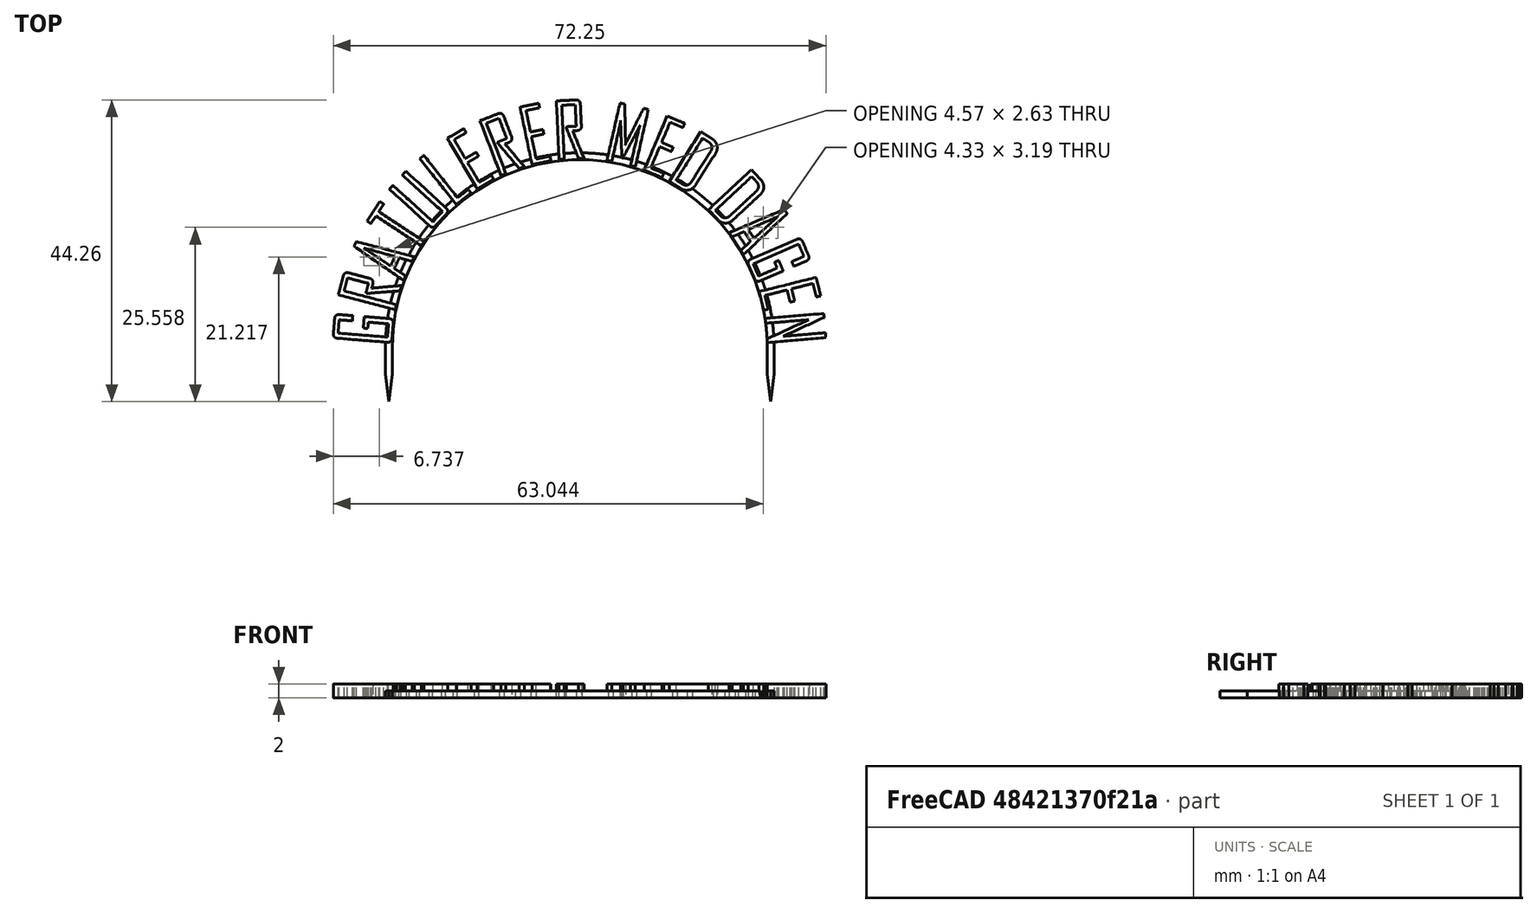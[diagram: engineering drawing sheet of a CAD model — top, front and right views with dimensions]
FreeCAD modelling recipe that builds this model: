
FCSTD DOCUMENT  (FreeCAD 0.20R29177 (Git))
Label: cake-topper-buon-compleanno
License: All rights reserved
LicenseURL: http://en.wikipedia.org/wiki/All_rights_reserved
objects: Part::Feature×22, Sketcher::SketchObject×4, PartDesign::Pad×4, App::DocumentObjectGroup×3, App::TextDocument×1, Spreadsheet::Sheet×1, PartDesign::Plane×1, PartDesign::Body×1, Mesh::Feature×1
note: 36 computed .brp shape members not serialized (recipe doc carries the construction recipe); baked Part::Feature solids carry a one-line shape summary decoded from their .brp

FEATURE [App::TextDocument] Text_document  label="Text document"
FEATURE [Spreadsheet::Sheet] Spreadsheet
  cells = A1=Text height; B1=text_h; C1(dim_text_h)==2mm; A2=Text offset x; B2=text_x; C2(dim_text_x)==-105.3mm; A3=Text offset y; B3=text_y; C3(dim_text_y)==177.4mm; A4=Scaffold height; B4=scaffold_h; C4(dim_scaffold_h)==1mm; A5=Scaffold width; B5=scaffold_w; C5(dim_scaffold_w)==1mm; A6=Scaffold inner radius; B6=scaffold_ir; C6(dim_scaffold_ir)==27.5mm; A7=Scaffold outer radius; B7=scaffold_or; C7(dim_scaffold_or)==dim_scaffold_ir + dim_scaffold_w; A8=Tines length; B8=tine_l; C8(dim_tine_l)==4mm; A9=Tines shaft length; B9=tine_shaft_l; C9(dim_tine_shaft_l)==4mm
FEATURE [PartDesign::Plane] DatumPlane  label="BaseXYDatumPlane"
  Length = 85.5553
  MapMode = 5
  ResizeMode = 0
  Support = -> [XY_Plane]
  Width = 74.5697
FEATURE [Sketcher::SketchObject] Sketch001  label="ArcSketch"
  FullyConstrained = true
  MapMode = 5
  Support = -> [DatumPlane]
  expr: Constraints[15] = Spreadsheet.dim_scaffold_or
  expr: Constraints[38] = Spreadsheet.dim_tine_shaft_l
  expr: Constraints[39] = Spreadsheet.dim_tine_l
  expr: Constraints[65] = Spreadsheet.dim_scaffold_or
  expr: Constraints[6] = Spreadsheet.dim_scaffold_ir
  sketch-geometry (26):
    g0: ArcOfCircle CenterX=0 CenterY=0 CenterZ=0 NormalX=0 NormalY=0 NormalZ=1 AngleXU=0 Radius=27.5 StartAngle=0 EndAngle=3.14159
    g1: LineSegment StartX=-28.5 StartY=3.5e-15 StartZ=0 EndX=-27.5 EndY=3.4e-15 EndZ=0
    g2: LineSegment StartX=27.5 StartY=0 StartZ=0 EndX=28.5 EndY=0 EndZ=0
    g3: ArcOfCircle CenterX=0 CenterY=0 CenterZ=0 NormalX=0 NormalY=0 NormalZ=1 AngleXU=0 Radius=28.5 StartAngle=1.44096 EndAngle=3.14159
    g4: ArcOfCircle CenterX=0 CenterY=0 CenterZ=0 NormalX=0 NormalY=0 NormalZ=1 AngleXU=0 Radius=28.5 StartAngle=0 EndAngle=1.40587
    g5: ArcOfCircle CenterX=0 CenterY=0 CenterZ=0 NormalX=0 NormalY=0 NormalZ=1 AngleXU=0 Radius=28.5 StartAngle=1.40587 EndAngle=1.44096
    g6: LineSegment StartX=3.69 StartY=28.2601 StartZ=0 EndX=5.12878 EndY=38.3822 EndZ=0
    g7: LineSegment StartX=4.67918 StartY=28.1133 StartZ=0 EndX=6.11883 EndY=38.2415 EndZ=0
    g8: LineSegment StartX=5.12878 StartY=38.3822 StartZ=0 EndX=6.11883 EndY=38.2415 EndZ=0
    g9: LineSegment StartX=-28.5 StartY=3.5e-15 StartZ=0 EndX=-28.5 EndY=-4 EndZ=0
    g10: LineSegment StartX=-27.5 StartY=3.4e-15 StartZ=0 EndX=-27.5 EndY=-4 EndZ=0
    g11: LineSegment StartX=-28.5 StartY=-4 StartZ=0 EndX=-28 EndY=-8 EndZ=0
    g12: LineSegment StartX=-27.5 StartY=-4 StartZ=0 EndX=-28 EndY=-8 EndZ=0
    g13: LineSegment StartX=-28.5 StartY=-4 StartZ=0 EndX=-28 EndY=-4 EndZ=0
    g14: LineSegment StartX=-28 StartY=-4 StartZ=0 EndX=-27.5 EndY=-4 EndZ=0
    g15: LineSegment StartX=-28 StartY=-4 StartZ=0 EndX=-28 EndY=-8 EndZ=0
    g16: LineSegment StartX=27.5 StartY=-4 StartZ=0 EndX=28 EndY=-4 EndZ=0
    g17: LineSegment StartX=28 StartY=-4 StartZ=0 EndX=28.5 EndY=-4 EndZ=0
    g18: LineSegment StartX=28 StartY=-4 StartZ=0 EndX=28 EndY=-8 EndZ=0
    g19: LineSegment StartX=27.5 StartY=0 StartZ=0 EndX=27.5 EndY=-4 EndZ=0
    g20: LineSegment StartX=28.5 StartY=0 StartZ=0 EndX=28.5 EndY=-4 EndZ=0
    g21: LineSegment StartX=27.5 StartY=-4 StartZ=0 EndX=28 EndY=-8 EndZ=0
    g22: LineSegment StartX=28.5 StartY=-4 StartZ=0 EndX=28 EndY=-8 EndZ=0
    g23: LineSegment StartX=3.69 StartY=28.2601 StartZ=0 EndX=0 EndY=28.2601 EndZ=0
    g24: LineSegment StartX=28.5 StartY=0 StartZ=0 EndX=28.5 EndY=28.5 EndZ=0
    g25: LineSegment StartX=28.5 StartY=28.5 StartZ=0 EndX=4.73415 EndY=28.5 EndZ=0
  constraints (71):
    c: Coincident(g0,g-1)
    c: PointOnObject(g0,g-1)
    c: PointOnObject(g0,g-1)
    c: Coincident(g4,g0)
    c: PointOnObject(g3,g-1)
    c: PointOnObject(g4,g-1)
    c: Radius(g0) = 27.5
    c: Coincident(g1,g3)
    c: Coincident(g1,g0)
    c: Coincident(g2,g0)
    c: Coincident(g2,g4)
    c: Coincident(g5,g3)
    c: Coincident(g4,g3)
    c: Coincident(g4,g5)
    c: Coincident(g4,g5)
    c: Radius(g4) = 28.5
    c: Coincident(g6,g3)
    c: Coincident(g7,g4)
    c: Coincident(g8,g6)
    c: Coincident(g8,g7)
    c: Parallel(g6,g7)
    c: Perpendicular(g8,g6)
    c: Coincident(g9,g3)
    c: Vertical(g9)
    c: Coincident(g10,g0)
    c: Vertical(g10)
    c: Coincident(g11,g9)
    c: Coincident(g12,g10)
    c: Coincident(g12,g11)
    c: Coincident(g13,g9)
    c: Horizontal(g13)
    c: Coincident(g14,g13)
    c: Coincident(g14,g10)
    c: Horizontal(g14)
    c: Coincident(g15,g13)
    c: Coincident(g15,g11)
    c: Equal(g14,g13)
    c: Vertical(g15)
    c: DistanceY(g10,g10) = 4
    c: DistanceY(g11,g10) = 4
    c: Horizontal(g16)
    c: Coincident(g17,g16)
    c: Horizontal(g17)
    c: Coincident(g18,g16)
    c: Vertical(g18)
    c: Coincident(g19,g0)
    c: Coincident(g19,g16)
    c: Vertical(g19)
    c: Coincident(g20,g4)
    c: Coincident(g20,g17)
    c: Vertical(g20)
    c: Coincident(g21,g19)
    c: Coincident(g21,g18)
    c: Coincident(g22,g20)
    c: Coincident(g22,g21)
    c: Equal(g19,g10)
    c: Equal(g18,g15)
    c: Equal(g17,g16)
    c: Distance(g8) = 1
    c: Coincident(g23,g3)
    c: PointOnObject(g23,g-2)
    c: Horizontal(g23)
    c: DistanceX(g23,g23) = 3.69
    c: Coincident(g24,g4)
    c: Vertical(g24)
    c: DistanceY(g24,g24) = 28.5
    c: Coincident(g25,g24)
    c: PointOnObject(g25,g7)
    c: Horizontal(g25)
    c: Angle(g25,g7) = 1.4296
    c: Distance(g7) = 10.23
FEATURE [PartDesign::Pad] Pad  label="ArcPad"
  Direction = (0,0,1)
  Length = 1
  Length2 = 10
  Profile = -> Sketch001
  ReferenceAxis = -> Sketch001 [N_Axis]
  Type = 0
  expr: Length = Spreadsheet.dim_scaffold_h
FEATURE [Part::Feature] path26706
  shape: bbox 8.818 x 4.113 x 2e-07 mm, 0 faces, 0 solids (baked)
FEATURE [Part::Feature] path26708
  shape: bbox 9.277 x 5.465 x 2e-07 mm, 0 faces, 0 solids (baked)
FEATURE [Part::Feature] path26710
  shape: bbox 8.816 x 5.676 x 2e-07 mm, 0 faces, 0 solids (baked)
FEATURE [Part::Feature] path26710001
  shape: bbox 4.566 x 2.632 x 2e-07 mm, 0 faces, 0 solids (baked)
FEATURE [Part::Feature] path26712
  shape: bbox 8.371 x 6.488 x 2e-07 mm, 0 faces, 0 solids (baked)
FEATURE [Part::Feature] path26714
  shape: bbox 8.547 x 8.23 x 2e-07 mm, 0 faces, 0 solids (baked)
FEATURE [Part::Feature] path26716
  shape: bbox 7.527 x 7.228 x 2e-07 mm, 0 faces, 0 solids (baked)
FEATURE [Part::Feature] path26718
  shape: bbox 6.804 x 8.859 x 2e-07 mm, 0 faces, 0 solids (baked)
FEATURE [Part::Feature] path26720
  shape: bbox 6.53 x 9.155 x 2e-07 mm, 0 faces, 0 solids (baked)
FEATURE [Part::Feature] path26722
  shape: bbox 4.54 x 9.017 x 2e-07 mm, 0 faces, 0 solids (baked)
FEATURE [Part::Feature] path26724
  shape: bbox 4.063 x 8.762 x 2e-07 mm, 0 faces, 0 solids (baked)
FEATURE [App::DocumentObjectGroup] Group  label="GratulererGroup"
  Group = -> [path26706,path26708,path26710,path26710001,path26712,path26714,path26716,path26718,path26720,path26722,path26724]
FEATURE [Part::Feature] path26726
  shape: bbox 6.071 x 9.357 x 2e-07 mm, 0 faces, 0 solids (baked)
FEATURE [Part::Feature] path26728
  shape: bbox 5.942 x 9.049 x 2e-07 mm, 0 faces, 0 solids (baked)
FEATURE [Part::Feature] path26730
  shape: bbox 7.088 x 8.663 x 2e-07 mm, 0 faces, 0 solids (baked)
FEATURE [Part::Feature] path26730001
  shape: bbox 5.278 x 6.906 x 2e-07 mm, 0 faces, 0 solids (baked)
FEATURE [App::DocumentObjectGroup] Group001  label="medGroup"
  Group = -> [path26726,path26728,path26730,path26730001]
FEATURE [Part::Feature] path26732
  shape: bbox 8.126 x 7.885 x 2e-07 mm, 0 faces, 0 solids (baked)
FEATURE [Part::Feature] path26732001
  shape: bbox 6.334 x 6.087 x 2e-07 mm, 0 faces, 0 solids (baked)
FEATURE [Part::Feature] path26734
  shape: bbox 8.492 x 6.647 x 2e-07 mm, 0 faces, 0 solids (baked)
FEATURE [Part::Feature] path26734001
  shape: bbox 4.328 x 3.192 x 2e-07 mm, 0 faces, 0 solids (baked)
FEATURE [Part::Feature] path26736
  shape: bbox 8.97 x 6.298 x 2e-07 mm, 0 faces, 0 solids (baked)
FEATURE [Part::Feature] path26738
  shape: bbox 9.049 x 4.849 x 2e-07 mm, 0 faces, 0 solids (baked)
FEATURE [Part::Feature] path26740
  shape: bbox 8.892 x 4.259 x 2e-07 mm, 0 faces, 0 solids (baked)
FEATURE [App::DocumentObjectGroup] Group002  label="dagenGroup"
  Group = -> [path26732,path26732001,path26734,path26734001,path26736,path26738,path26740]
FEATURE [Sketcher::SketchObject] Sketch  label="GratulererSketch"
  FullyConstrained = false
  Placement = pos=(-105.3,177.4,0) rot=(0,0,1;0rad)
  expr: .Placement.Base.x = Spreadsheet.dim_text_x
  expr: .Placement.Base.y = Spreadsheet.dim_text_y
  sketch-geometry (138):
    g0: BSplineCurve PolesCount=3 KnotsCount=2 Degree=2 IsPeriodic=0
    g1: BSplineCurve PolesCount=3 KnotsCount=2 Degree=2 IsPeriodic=0
    g2: BSplineCurve PolesCount=2 KnotsCount=2 Degree=1 IsPeriodic=0
    g3: BSplineCurve PolesCount=3 KnotsCount=2 Degree=2 IsPeriodic=0
    g4: BSplineCurve PolesCount=3 KnotsCount=2 Degree=2 IsPeriodic=0
    g5: BSplineCurve PolesCount=2 KnotsCount=2 Degree=1 IsPeriodic=0
    g6: BSplineCurve PolesCount=3 KnotsCount=2 Degree=2 IsPeriodic=0
    g7: BSplineCurve PolesCount=3 KnotsCount=2 Degree=2 IsPeriodic=0
    g8: BSplineCurve PolesCount=2 KnotsCount=2 Degree=1 IsPeriodic=0
    g9: BSplineCurve PolesCount=3 KnotsCount=2 Degree=2 IsPeriodic=0
    g10: BSplineCurve PolesCount=3 KnotsCount=2 Degree=2 IsPeriodic=0
    g11: BSplineCurve PolesCount=2 KnotsCount=2 Degree=1 IsPeriodic=0
    g12: BSplineCurve PolesCount=2 KnotsCount=2 Degree=1 IsPeriodic=0
    g13: BSplineCurve PolesCount=2 KnotsCount=2 Degree=1 IsPeriodic=0
    g14: BSplineCurve PolesCount=2 KnotsCount=2 Degree=1 IsPeriodic=0
    g15: BSplineCurve PolesCount=2 KnotsCount=2 Degree=1 IsPeriodic=0
    g16: BSplineCurve PolesCount=2 KnotsCount=2 Degree=1 IsPeriodic=0
    g17: BSplineCurve PolesCount=2 KnotsCount=2 Degree=1 IsPeriodic=0
    g18: BSplineCurve PolesCount=2 KnotsCount=2 Degree=1 IsPeriodic=0
    g19: BSplineCurve PolesCount=2 KnotsCount=2 Degree=1 IsPeriodic=0
    g20: BSplineCurve PolesCount=2 KnotsCount=2 Degree=1 IsPeriodic=0
    g21: BSplineCurve PolesCount=2 KnotsCount=2 Degree=1 IsPeriodic=0
    g22: BSplineCurve PolesCount=2 KnotsCount=2 Degree=1 IsPeriodic=0
    g23: BSplineCurve PolesCount=2 KnotsCount=2 Degree=1 IsPeriodic=0
    g24: BSplineCurve PolesCount=2 KnotsCount=2 Degree=1 IsPeriodic=0
    g25: BSplineCurve PolesCount=2 KnotsCount=2 Degree=1 IsPeriodic=0
    g26: BSplineCurve PolesCount=2 KnotsCount=2 Degree=1 IsPeriodic=0
    g27: BSplineCurve PolesCount=2 KnotsCount=2 Degree=1 IsPeriodic=0
    g28: BSplineCurve PolesCount=2 KnotsCount=2 Degree=1 IsPeriodic=0
    g29: BSplineCurve PolesCount=2 KnotsCount=2 Degree=1 IsPeriodic=0
    g30: BSplineCurve PolesCount=2 KnotsCount=2 Degree=1 IsPeriodic=0
    g31: BSplineCurve PolesCount=2 KnotsCount=2 Degree=1 IsPeriodic=0
    g32: BSplineCurve PolesCount=3 KnotsCount=2 Degree=2 IsPeriodic=0
    g33: BSplineCurve PolesCount=3 KnotsCount=2 Degree=2 IsPeriodic=0
    g34: BSplineCurve PolesCount=2 KnotsCount=2 Degree=1 IsPeriodic=0
    g35: BSplineCurve PolesCount=3 KnotsCount=2 Degree=2 IsPeriodic=0
    g36: BSplineCurve PolesCount=3 KnotsCount=2 Degree=2 IsPeriodic=0
    g37: BSplineCurve PolesCount=3 KnotsCount=2 Degree=2 IsPeriodic=0
    g38: BSplineCurve PolesCount=3 KnotsCount=2 Degree=2 IsPeriodic=0
    g39: BSplineCurve PolesCount=2 KnotsCount=2 Degree=1 IsPeriodic=0
    g40: BSplineCurve PolesCount=2 KnotsCount=2 Degree=1 IsPeriodic=0
    g41: BSplineCurve PolesCount=2 KnotsCount=2 Degree=1 IsPeriodic=0
    g42: BSplineCurve PolesCount=2 KnotsCount=2 Degree=1 IsPeriodic=0
    g43: BSplineCurve PolesCount=2 KnotsCount=2 Degree=1 IsPeriodic=0
    g44: BSplineCurve PolesCount=2 KnotsCount=2 Degree=1 IsPeriodic=0
    g45: BSplineCurve PolesCount=2 KnotsCount=2 Degree=1 IsPeriodic=0
    g46: BSplineCurve PolesCount=2 KnotsCount=2 Degree=1 IsPeriodic=0
    g47: BSplineCurve PolesCount=2 KnotsCount=2 Degree=1 IsPeriodic=0
    g48: BSplineCurve PolesCount=2 KnotsCount=2 Degree=1 IsPeriodic=0
    g49: BSplineCurve PolesCount=2 KnotsCount=2 Degree=1 IsPeriodic=0
    g50: BSplineCurve PolesCount=2 KnotsCount=2 Degree=1 IsPeriodic=0
    g51: BSplineCurve PolesCount=2 KnotsCount=2 Degree=1 IsPeriodic=0
    g52: BSplineCurve PolesCount=2 KnotsCount=2 Degree=1 IsPeriodic=0
    g53: BSplineCurve PolesCount=2 KnotsCount=2 Degree=1 IsPeriodic=0
    g54: BSplineCurve PolesCount=2 KnotsCount=2 Degree=1 IsPeriodic=0
    g55: BSplineCurve PolesCount=2 KnotsCount=2 Degree=1 IsPeriodic=0
    g56: BSplineCurve PolesCount=2 KnotsCount=2 Degree=1 IsPeriodic=0
    g57: BSplineCurve PolesCount=2 KnotsCount=2 Degree=1 IsPeriodic=0
    g58: BSplineCurve PolesCount=2 KnotsCount=2 Degree=1 IsPeriodic=0
    g59: BSplineCurve PolesCount=2 KnotsCount=2 Degree=1 IsPeriodic=0
    g60: BSplineCurve PolesCount=3 KnotsCount=2 Degree=2 IsPeriodic=0
    g61: BSplineCurve PolesCount=3 KnotsCount=2 Degree=2 IsPeriodic=0
    g62: BSplineCurve PolesCount=2 KnotsCount=2 Degree=1 IsPeriodic=0
    g63: BSplineCurve PolesCount=3 KnotsCount=2 Degree=2 IsPeriodic=0
    g64: BSplineCurve PolesCount=3 KnotsCount=2 Degree=2 IsPeriodic=0
    g65: BSplineCurve PolesCount=2 KnotsCount=2 Degree=1 IsPeriodic=0
    g66: BSplineCurve PolesCount=2 KnotsCount=2 Degree=1 IsPeriodic=0
    g67: BSplineCurve PolesCount=2 KnotsCount=2 Degree=1 IsPeriodic=0
    g68: BSplineCurve PolesCount=2 KnotsCount=2 Degree=1 IsPeriodic=0
    g69: BSplineCurve PolesCount=2 KnotsCount=2 Degree=1 IsPeriodic=0
    g70: BSplineCurve PolesCount=2 KnotsCount=2 Degree=1 IsPeriodic=0
    g71: BSplineCurve PolesCount=2 KnotsCount=2 Degree=1 IsPeriodic=0
    g72: BSplineCurve PolesCount=2 KnotsCount=2 Degree=1 IsPeriodic=0
    g73: BSplineCurve PolesCount=2 KnotsCount=2 Degree=1 IsPeriodic=0
    g74: BSplineCurve PolesCount=2 KnotsCount=2 Degree=1 IsPeriodic=0
    g75: BSplineCurve PolesCount=2 KnotsCount=2 Degree=1 IsPeriodic=0
    g76: BSplineCurve PolesCount=2 KnotsCount=2 Degree=1 IsPeriodic=0
    g77: BSplineCurve PolesCount=2 KnotsCount=2 Degree=1 IsPeriodic=0
    g78: BSplineCurve PolesCount=2 KnotsCount=2 Degree=1 IsPeriodic=0
    g79: BSplineCurve PolesCount=2 KnotsCount=2 Degree=1 IsPeriodic=0
    g80: BSplineCurve PolesCount=2 KnotsCount=2 Degree=1 IsPeriodic=0
    g81: BSplineCurve PolesCount=2 KnotsCount=2 Degree=1 IsPeriodic=0
    g82: BSplineCurve PolesCount=2 KnotsCount=2 Degree=1 IsPeriodic=0
    g83: BSplineCurve PolesCount=2 KnotsCount=2 Degree=1 IsPeriodic=0
    g84: BSplineCurve PolesCount=2 KnotsCount=2 Degree=1 IsPeriodic=0
    g85: BSplineCurve PolesCount=2 KnotsCount=2 Degree=1 IsPeriodic=0
    g86: BSplineCurve PolesCount=2 KnotsCount=2 Degree=1 IsPeriodic=0
    g87: BSplineCurve PolesCount=2 KnotsCount=2 Degree=1 IsPeriodic=0
    g88: BSplineCurve PolesCount=2 KnotsCount=2 Degree=1 IsPeriodic=0
    g89: BSplineCurve PolesCount=2 KnotsCount=2 Degree=1 IsPeriodic=0
    g90: BSplineCurve PolesCount=2 KnotsCount=2 Degree=1 IsPeriodic=0
    g91: BSplineCurve PolesCount=2 KnotsCount=2 Degree=1 IsPeriodic=0
    g92: BSplineCurve PolesCount=2 KnotsCount=2 Degree=1 IsPeriodic=0
    g93: BSplineCurve PolesCount=2 KnotsCount=2 Degree=1 IsPeriodic=0
    g94: BSplineCurve PolesCount=2 KnotsCount=2 Degree=1 IsPeriodic=0
    g95: BSplineCurve PolesCount=2 KnotsCount=2 Degree=1 IsPeriodic=0
    g96: BSplineCurve PolesCount=2 KnotsCount=2 Degree=1 IsPeriodic=0
    g97: BSplineCurve PolesCount=2 KnotsCount=2 Degree=1 IsPeriodic=0
    g98: BSplineCurve PolesCount=2 KnotsCount=2 Degree=1 IsPeriodic=0
    g99: BSplineCurve PolesCount=2 KnotsCount=2 Degree=1 IsPeriodic=0
    g100: BSplineCurve PolesCount=3 KnotsCount=2 Degree=2 IsPeriodic=0
    g101: BSplineCurve PolesCount=3 KnotsCount=2 Degree=2 IsPeriodic=0
    g102: BSplineCurve PolesCount=2 KnotsCount=2 Degree=1 IsPeriodic=0
    g103: BSplineCurve PolesCount=3 KnotsCount=2 Degree=2 IsPeriodic=0
    g104: BSplineCurve PolesCount=3 KnotsCount=2 Degree=2 IsPeriodic=0
    g105: BSplineCurve PolesCount=3 KnotsCount=2 Degree=2 IsPeriodic=0
    g106: BSplineCurve PolesCount=3 KnotsCount=2 Degree=2 IsPeriodic=0
    g107: BSplineCurve PolesCount=2 KnotsCount=2 Degree=1 IsPeriodic=0
    g108: BSplineCurve PolesCount=2 KnotsCount=2 Degree=1 IsPeriodic=0
    g109: BSplineCurve PolesCount=2 KnotsCount=2 Degree=1 IsPeriodic=0
    g110: BSplineCurve PolesCount=2 KnotsCount=2 Degree=1 IsPeriodic=0
    g111: BSplineCurve PolesCount=2 KnotsCount=2 Degree=1 IsPeriodic=0
    g112: BSplineCurve PolesCount=2 KnotsCount=2 Degree=1 IsPeriodic=0
    g113: BSplineCurve PolesCount=2 KnotsCount=2 Degree=1 IsPeriodic=0
    g114: BSplineCurve PolesCount=2 KnotsCount=2 Degree=1 IsPeriodic=0
    g115: BSplineCurve PolesCount=2 KnotsCount=2 Degree=1 IsPeriodic=0
    g116: BSplineCurve PolesCount=2 KnotsCount=2 Degree=1 IsPeriodic=0
    g117: BSplineCurve PolesCount=2 KnotsCount=2 Degree=1 IsPeriodic=0
    g118: BSplineCurve PolesCount=2 KnotsCount=2 Degree=1 IsPeriodic=0
    g119: BSplineCurve PolesCount=2 KnotsCount=2 Degree=1 IsPeriodic=0
    g120: BSplineCurve PolesCount=2 KnotsCount=2 Degree=1 IsPeriodic=0
    g121: BSplineCurve PolesCount=2 KnotsCount=2 Degree=1 IsPeriodic=0
    g122: BSplineCurve PolesCount=2 KnotsCount=2 Degree=1 IsPeriodic=0
    g123: BSplineCurve PolesCount=2 KnotsCount=2 Degree=1 IsPeriodic=0
    g124: BSplineCurve PolesCount=2 KnotsCount=2 Degree=1 IsPeriodic=0
    g125: BSplineCurve PolesCount=2 KnotsCount=2 Degree=1 IsPeriodic=0
    g126: BSplineCurve PolesCount=2 KnotsCount=2 Degree=1 IsPeriodic=0
    g127: BSplineCurve PolesCount=2 KnotsCount=2 Degree=1 IsPeriodic=0
    g128: BSplineCurve PolesCount=2 KnotsCount=2 Degree=1 IsPeriodic=0
    g129: BSplineCurve PolesCount=2 KnotsCount=2 Degree=1 IsPeriodic=0
    g130: BSplineCurve PolesCount=3 KnotsCount=2 Degree=2 IsPeriodic=0
    g131: BSplineCurve PolesCount=3 KnotsCount=2 Degree=2 IsPeriodic=0
    g132: BSplineCurve PolesCount=2 KnotsCount=2 Degree=1 IsPeriodic=0
    g133: BSplineCurve PolesCount=3 KnotsCount=2 Degree=2 IsPeriodic=0
    g134: BSplineCurve PolesCount=3 KnotsCount=2 Degree=2 IsPeriodic=0
    g135: BSplineCurve PolesCount=3 KnotsCount=2 Degree=2 IsPeriodic=0
    g136: BSplineCurve PolesCount=3 KnotsCount=2 Degree=2 IsPeriodic=0
    g137: BSplineCurve PolesCount=2 KnotsCount=2 Degree=1 IsPeriodic=0
  constraints (138):
    c: Coincident(g0,g1)
    c: Coincident(g1,g2)
    c: Coincident(g2,g3)
    c: Coincident(g3,g4)
    c: Coincident(g4,g5)
    c: Coincident(g5,g6)
    c: Coincident(g6,g7)
    c: Coincident(g7,g8)
    c: Coincident(g8,g9)
    c: Coincident(g9,g10)
    c: Coincident(g10,g11)
    c: Coincident(g11,g12)
    c: Coincident(g12,g13)
    c: Coincident(g13,g14)
    c: Coincident(g14,g15)
    c: Coincident(g15,g16)
    c: Coincident(g16,g17)
    c: Coincident(g17,g18)
    c: Coincident(g18,g19)
    c: Coincident(g19,g20)
    c: Coincident(g20,g21)
    c: Coincident(g21,g0)
    c: Coincident(g22,g23)
    c: Coincident(g23,g24)
    c: Coincident(g24,g25)
    c: Coincident(g25,g26)
    c: Coincident(g26,g27)
    c: Coincident(g27,g28)
    c: Coincident(g28,g29)
    c: Coincident(g29,g30)
    c: Coincident(g30,g31)
    c: Coincident(g31,g32)
    c: Coincident(g32,g33)
    c: Coincident(g33,g34)
    c: Coincident(g34,g35)
    c: Coincident(g35,g36)
    c: Coincident(g36,g37)
    c: Coincident(g37,g38)
    c: Coincident(g38,g39)
    c: Coincident(g39,g22)
    c: Coincident(g40,g41)
    c: Coincident(g41,g42)
    c: Coincident(g42,g43)
    c: Coincident(g43,g44)
    c: Coincident(g44,g45)
    c: Coincident(g45,g46)
    c: Coincident(g46,g47)
    c: Coincident(g47,g48)
    c: Coincident(g48,g40)
    c: Coincident(g49,g50)
    c: Coincident(g50,g51)
    c: Coincident(g51,g49)
    c: Coincident(g52,g53)
    c: Coincident(g53,g54)
    c: Coincident(g54,g55)
    c: Coincident(g55,g56)
    c: Coincident(g56,g57)
    c: Coincident(g57,g58)
    c: Coincident(g58,g59)
    c: Coincident(g59,g52)
    c: Coincident(g60,g61)
    c: Coincident(g61,g62)
    c: Coincident(g62,g63)
    c: Coincident(g63,g64)
    c: Coincident(g64,g65)
    c: Coincident(g65,g66)
    c: Coincident(g66,g67)
    c: Coincident(g67,g68)
    c: Coincident(g68,g69)
    c: Coincident(g69,g70)
    c: Coincident(g70,g71)
    c: Coincident(g71,g60)
    c: Coincident(g72,g73)
    c: Coincident(g73,g74)
    c: Coincident(g74,g75)
    c: Coincident(g75,g76)
    c: Coincident(g76,g77)
    c: Coincident(g77,g72)
    c: Coincident(g78,g79)
    c: Coincident(g79,g80)
    c: Coincident(g80,g81)
    c: Coincident(g81,g82)
    c: Coincident(g82,g83)
    c: Coincident(g83,g84)
    c: Coincident(g84,g85)
    c: Coincident(g85,g86)
    c: Coincident(g86,g87)
    c: Coincident(g87,g88)
    c: Coincident(g88,g89)
    c: Coincident(g89,g78)
    c: Coincident(g90,g91)
    c: Coincident(g91,g92)
    c: Coincident(g92,g93)
    c: Coincident(g93,g94)
    c: Coincident(g94,g95)
    c: Coincident(g95,g96)
    c: Coincident(g96,g97)
    c: Coincident(g97,g98)
    c: Coincident(g98,g99)
    c: Coincident(g99,g100)
    c: Coincident(g100,g101)
    c: Coincident(g101,g102)
    c: Coincident(g102,g103)
    c: Coincident(g103,g104)
    c: Coincident(g104,g105)
    c: Coincident(g105,g106)
    c: Coincident(g106,g107)
    c: Coincident(g107,g90)
    c: Coincident(g108,g109)
    c: Coincident(g109,g110)
    c: Coincident(g110,g111)
    c: Coincident(g111,g112)
    c: Coincident(g112,g113)
    c: Coincident(g113,g114)
    c: Coincident(g114,g115)
    c: Coincident(g115,g116)
    c: Coincident(g116,g117)
    c: Coincident(g117,g118)
    c: Coincident(g118,g119)
    c: Coincident(g119,g108)
    c: Coincident(g120,g121)
    c: Coincident(g121,g122)
    c: Coincident(g122,g123)
    c: Coincident(g123,g124)
    c: Coincident(g124,g125)
    c: Coincident(g125,g126)
    c: Coincident(g126,g127)
    c: Coincident(g127,g128)
    c: Coincident(g128,g129)
    c: Coincident(g129,g130)
    c: Coincident(g130,g131)
    c: Coincident(g131,g132)
    c: Coincident(g132,g133)
    c: Coincident(g133,g134)
    c: Coincident(g134,g135)
    c: Coincident(g135,g136)
    c: Coincident(g136,g137)
    c: Coincident(g137,g120)
FEATURE [Sketcher::SketchObject] Sketch002  label="MedSketch"
  FullyConstrained = false
  Placement = pos=(-105.3,177.4,0) rot=(0,0,1;0rad)
  expr: .Placement.Base.x = Spreadsheet.dim_text_x
  expr: .Placement.Base.y = Spreadsheet.dim_text_y
  sketch-geometry (45):
    g0: BSplineCurve PolesCount=2 KnotsCount=2 Degree=1 IsPeriodic=0
    g1: BSplineCurve PolesCount=2 KnotsCount=2 Degree=1 IsPeriodic=0
    g2: BSplineCurve PolesCount=3 KnotsCount=2 Degree=2 IsPeriodic=0
    g3: BSplineCurve PolesCount=2 KnotsCount=2 Degree=1 IsPeriodic=0
    g4: BSplineCurve PolesCount=2 KnotsCount=2 Degree=1 IsPeriodic=0
    g5: BSplineCurve PolesCount=2 KnotsCount=2 Degree=1 IsPeriodic=0
    g6: BSplineCurve PolesCount=3 KnotsCount=2 Degree=2 IsPeriodic=0
    g7: BSplineCurve PolesCount=2 KnotsCount=2 Degree=1 IsPeriodic=0
    g8: BSplineCurve PolesCount=2 KnotsCount=2 Degree=1 IsPeriodic=0
    g9: BSplineCurve PolesCount=2 KnotsCount=2 Degree=1 IsPeriodic=0
    g10: BSplineCurve PolesCount=2 KnotsCount=2 Degree=1 IsPeriodic=0
    g11: BSplineCurve PolesCount=2 KnotsCount=2 Degree=1 IsPeriodic=0
    g12: BSplineCurve PolesCount=3 KnotsCount=2 Degree=2 IsPeriodic=0
    g13: BSplineCurve PolesCount=3 KnotsCount=2 Degree=2 IsPeriodic=0
    g14: BSplineCurve PolesCount=2 KnotsCount=2 Degree=1 IsPeriodic=0
    g15: BSplineCurve PolesCount=2 KnotsCount=2 Degree=1 IsPeriodic=0
    g16: BSplineCurve PolesCount=2 KnotsCount=2 Degree=1 IsPeriodic=0
    g17: BSplineCurve PolesCount=2 KnotsCount=2 Degree=1 IsPeriodic=0
    g18: BSplineCurve PolesCount=2 KnotsCount=2 Degree=1 IsPeriodic=0
    g19: BSplineCurve PolesCount=2 KnotsCount=2 Degree=1 IsPeriodic=0
    g20: BSplineCurve PolesCount=2 KnotsCount=2 Degree=1 IsPeriodic=0
    g21: BSplineCurve PolesCount=2 KnotsCount=2 Degree=1 IsPeriodic=0
    g22: BSplineCurve PolesCount=2 KnotsCount=2 Degree=1 IsPeriodic=0
    g23: BSplineCurve PolesCount=2 KnotsCount=2 Degree=1 IsPeriodic=0
    g24: BSplineCurve PolesCount=2 KnotsCount=2 Degree=1 IsPeriodic=0
    g25: BSplineCurve PolesCount=2 KnotsCount=2 Degree=1 IsPeriodic=0
    g26: BSplineCurve PolesCount=2 KnotsCount=2 Degree=1 IsPeriodic=0
    g27: BSplineCurve PolesCount=2 KnotsCount=2 Degree=1 IsPeriodic=0
    g28: BSplineCurve PolesCount=2 KnotsCount=2 Degree=1 IsPeriodic=0
    g29: BSplineCurve PolesCount=3 KnotsCount=2 Degree=2 IsPeriodic=0
    g30: BSplineCurve PolesCount=3 KnotsCount=2 Degree=2 IsPeriodic=0
    g31: BSplineCurve PolesCount=2 KnotsCount=2 Degree=1 IsPeriodic=0
    g32: BSplineCurve PolesCount=2 KnotsCount=2 Degree=1 IsPeriodic=0
    g33: BSplineCurve PolesCount=2 KnotsCount=2 Degree=1 IsPeriodic=0
    g34: BSplineCurve PolesCount=3 KnotsCount=2 Degree=2 IsPeriodic=0
    g35: BSplineCurve PolesCount=3 KnotsCount=2 Degree=2 IsPeriodic=0
    g36: BSplineCurve PolesCount=2 KnotsCount=2 Degree=1 IsPeriodic=0
    g37: BSplineCurve PolesCount=2 KnotsCount=2 Degree=1 IsPeriodic=0
    g38: BSplineCurve PolesCount=3 KnotsCount=2 Degree=2 IsPeriodic=0
    g39: BSplineCurve PolesCount=3 KnotsCount=2 Degree=2 IsPeriodic=0
    g40: BSplineCurve PolesCount=2 KnotsCount=2 Degree=1 IsPeriodic=0
    g41: BSplineCurve PolesCount=2 KnotsCount=2 Degree=1 IsPeriodic=0
    g42: BSplineCurve PolesCount=2 KnotsCount=2 Degree=1 IsPeriodic=0
    g43: BSplineCurve PolesCount=3 KnotsCount=2 Degree=2 IsPeriodic=0
    g44: BSplineCurve PolesCount=3 KnotsCount=2 Degree=2 IsPeriodic=0
  constraints (45):
    c: Coincident(g0,g1)
    c: Coincident(g1,g2)
    c: Coincident(g2,g3)
    c: Coincident(g3,g4)
    c: Coincident(g4,g5)
    c: Coincident(g5,g6)
    c: Coincident(g6,g7)
    c: Coincident(g7,g8)
    c: Coincident(g8,g9)
    c: Coincident(g9,g10)
    c: Coincident(g10,g11)
    c: Coincident(g11,g12)
    c: Coincident(g12,g13)
    c: Coincident(g13,g14)
    c: Coincident(g14,g15)
    c: Coincident(g15,g16)
    c: Coincident(g16,g0)
    c: Coincident(g17,g18)
    c: Coincident(g18,g19)
    c: Coincident(g19,g20)
    c: Coincident(g20,g21)
    c: Coincident(g21,g22)
    c: Coincident(g22,g23)
    c: Coincident(g23,g24)
    c: Coincident(g24,g25)
    c: Coincident(g25,g26)
    c: Coincident(g26,g27)
    c: Coincident(g27,g28)
    c: Coincident(g28,g17)
    c: Coincident(g29,g30)
    c: Coincident(g30,g31)
    c: Coincident(g31,g32)
    c: Coincident(g32,g33)
    c: Coincident(g33,g34)
    c: Coincident(g34,g35)
    c: Coincident(g35,g36)
    c: Coincident(g36,g29)
    c: Coincident(g37,g38)
    c: Coincident(g38,g39)
    c: Coincident(g39,g40)
    c: Coincident(g40,g41)
    c: Coincident(g41,g42)
    c: Coincident(g42,g43)
    c: Coincident(g43,g44)
    c: Coincident(g44,g37)
FEATURE [Sketcher::SketchObject] Sketch003  label="DagenSketch"
  FullyConstrained = false
  Placement = pos=(-105.3,177.4,0) rot=(0,0,1;0rad)
  expr: .Placement.Base.x = Spreadsheet.dim_text_x
  expr: .Placement.Base.y = Spreadsheet.dim_text_y
  sketch-geometry (72):
    g0: BSplineCurve PolesCount=3 KnotsCount=2 Degree=2 IsPeriodic=0
    g1: BSplineCurve PolesCount=3 KnotsCount=2 Degree=2 IsPeriodic=0
    g2: BSplineCurve PolesCount=2 KnotsCount=2 Degree=1 IsPeriodic=0
    g3: BSplineCurve PolesCount=2 KnotsCount=2 Degree=1 IsPeriodic=0
    g4: BSplineCurve PolesCount=2 KnotsCount=2 Degree=1 IsPeriodic=0
    g5: BSplineCurve PolesCount=3 KnotsCount=2 Degree=2 IsPeriodic=0
    g6: BSplineCurve PolesCount=3 KnotsCount=2 Degree=2 IsPeriodic=0
    g7: BSplineCurve PolesCount=2 KnotsCount=2 Degree=1 IsPeriodic=0
    g8: BSplineCurve PolesCount=2 KnotsCount=2 Degree=1 IsPeriodic=0
    g9: BSplineCurve PolesCount=3 KnotsCount=2 Degree=2 IsPeriodic=0
    g10: BSplineCurve PolesCount=3 KnotsCount=2 Degree=2 IsPeriodic=0
    g11: BSplineCurve PolesCount=2 KnotsCount=2 Degree=1 IsPeriodic=0
    g12: BSplineCurve PolesCount=2 KnotsCount=2 Degree=1 IsPeriodic=0
    g13: BSplineCurve PolesCount=2 KnotsCount=2 Degree=1 IsPeriodic=0
    g14: BSplineCurve PolesCount=3 KnotsCount=2 Degree=2 IsPeriodic=0
    g15: BSplineCurve PolesCount=3 KnotsCount=2 Degree=2 IsPeriodic=0
    g16: BSplineCurve PolesCount=2 KnotsCount=2 Degree=1 IsPeriodic=0
    g17: BSplineCurve PolesCount=2 KnotsCount=2 Degree=1 IsPeriodic=0
    g18: BSplineCurve PolesCount=2 KnotsCount=2 Degree=1 IsPeriodic=0
    g19: BSplineCurve PolesCount=2 KnotsCount=2 Degree=1 IsPeriodic=0
    g20: BSplineCurve PolesCount=2 KnotsCount=2 Degree=1 IsPeriodic=0
    g21: BSplineCurve PolesCount=2 KnotsCount=2 Degree=1 IsPeriodic=0
    g22: BSplineCurve PolesCount=2 KnotsCount=2 Degree=1 IsPeriodic=0
    g23: BSplineCurve PolesCount=2 KnotsCount=2 Degree=1 IsPeriodic=0
    g24: BSplineCurve PolesCount=2 KnotsCount=2 Degree=1 IsPeriodic=0
    g25: BSplineCurve PolesCount=2 KnotsCount=2 Degree=1 IsPeriodic=0
    g26: BSplineCurve PolesCount=2 KnotsCount=2 Degree=1 IsPeriodic=0
    g27: BSplineCurve PolesCount=2 KnotsCount=2 Degree=1 IsPeriodic=0
    g28: BSplineCurve PolesCount=3 KnotsCount=2 Degree=2 IsPeriodic=0
    g29: BSplineCurve PolesCount=3 KnotsCount=2 Degree=2 IsPeriodic=0
    g30: BSplineCurve PolesCount=2 KnotsCount=2 Degree=1 IsPeriodic=0
    g31: BSplineCurve PolesCount=3 KnotsCount=2 Degree=2 IsPeriodic=0
    g32: BSplineCurve PolesCount=3 KnotsCount=2 Degree=2 IsPeriodic=0
    g33: BSplineCurve PolesCount=2 KnotsCount=2 Degree=1 IsPeriodic=0
    g34: BSplineCurve PolesCount=3 KnotsCount=2 Degree=2 IsPeriodic=0
    g35: BSplineCurve PolesCount=3 KnotsCount=2 Degree=2 IsPeriodic=0
    g36: BSplineCurve PolesCount=2 KnotsCount=2 Degree=1 IsPeriodic=0
    g37: BSplineCurve PolesCount=3 KnotsCount=2 Degree=2 IsPeriodic=0
    g38: BSplineCurve PolesCount=3 KnotsCount=2 Degree=2 IsPeriodic=0
    g39: BSplineCurve PolesCount=2 KnotsCount=2 Degree=1 IsPeriodic=0
    g40: BSplineCurve PolesCount=2 KnotsCount=2 Degree=1 IsPeriodic=0
    g41: BSplineCurve PolesCount=2 KnotsCount=2 Degree=1 IsPeriodic=0
    g42: BSplineCurve PolesCount=2 KnotsCount=2 Degree=1 IsPeriodic=0
    g43: BSplineCurve PolesCount=2 KnotsCount=2 Degree=1 IsPeriodic=0
    g44: BSplineCurve PolesCount=2 KnotsCount=2 Degree=1 IsPeriodic=0
    g45: BSplineCurve PolesCount=2 KnotsCount=2 Degree=1 IsPeriodic=0
    g46: BSplineCurve PolesCount=2 KnotsCount=2 Degree=1 IsPeriodic=0
    g47: BSplineCurve PolesCount=2 KnotsCount=2 Degree=1 IsPeriodic=0
    g48: BSplineCurve PolesCount=2 KnotsCount=2 Degree=1 IsPeriodic=0
    g49: BSplineCurve PolesCount=2 KnotsCount=2 Degree=1 IsPeriodic=0
    g50: BSplineCurve PolesCount=2 KnotsCount=2 Degree=1 IsPeriodic=0
    g51: BSplineCurve PolesCount=2 KnotsCount=2 Degree=1 IsPeriodic=0
    g52: BSplineCurve PolesCount=2 KnotsCount=2 Degree=1 IsPeriodic=0
    g53: BSplineCurve PolesCount=2 KnotsCount=2 Degree=1 IsPeriodic=0
    g54: BSplineCurve PolesCount=2 KnotsCount=2 Degree=1 IsPeriodic=0
    g55: BSplineCurve PolesCount=2 KnotsCount=2 Degree=1 IsPeriodic=0
    g56: BSplineCurve PolesCount=2 KnotsCount=2 Degree=1 IsPeriodic=0
    g57: BSplineCurve PolesCount=2 KnotsCount=2 Degree=1 IsPeriodic=0
    g58: BSplineCurve PolesCount=2 KnotsCount=2 Degree=1 IsPeriodic=0
    g59: BSplineCurve PolesCount=2 KnotsCount=2 Degree=1 IsPeriodic=0
    g60: BSplineCurve PolesCount=2 KnotsCount=2 Degree=1 IsPeriodic=0
    g61: BSplineCurve PolesCount=2 KnotsCount=2 Degree=1 IsPeriodic=0
    g62: BSplineCurve PolesCount=2 KnotsCount=2 Degree=1 IsPeriodic=0
    g63: BSplineCurve PolesCount=2 KnotsCount=2 Degree=1 IsPeriodic=0
    g64: BSplineCurve PolesCount=2 KnotsCount=2 Degree=1 IsPeriodic=0
    g65: BSplineCurve PolesCount=2 KnotsCount=2 Degree=1 IsPeriodic=0
    g66: BSplineCurve PolesCount=2 KnotsCount=2 Degree=1 IsPeriodic=0
    g67: BSplineCurve PolesCount=2 KnotsCount=2 Degree=1 IsPeriodic=0
    g68: BSplineCurve PolesCount=2 KnotsCount=2 Degree=1 IsPeriodic=0
    g69: BSplineCurve PolesCount=2 KnotsCount=2 Degree=1 IsPeriodic=0
    g70: BSplineCurve PolesCount=2 KnotsCount=2 Degree=1 IsPeriodic=0
    g71: BSplineCurve PolesCount=2 KnotsCount=2 Degree=1 IsPeriodic=0
  constraints (72):
    c: Coincident(g0,g1)
    c: Coincident(g1,g2)
    c: Coincident(g2,g3)
    c: Coincident(g3,g4)
    c: Coincident(g4,g5)
    c: Coincident(g5,g6)
    c: Coincident(g6,g7)
    c: Coincident(g7,g0)
    c: Coincident(g8,g9)
    c: Coincident(g9,g10)
    c: Coincident(g10,g11)
    c: Coincident(g11,g12)
    c: Coincident(g12,g13)
    c: Coincident(g13,g14)
    c: Coincident(g14,g15)
    c: Coincident(g15,g8)
    c: Coincident(g16,g17)
    c: Coincident(g17,g18)
    c: Coincident(g18,g19)
    c: Coincident(g19,g20)
    c: Coincident(g20,g21)
    c: Coincident(g21,g22)
    c: Coincident(g22,g23)
    c: Coincident(g23,g24)
    c: Coincident(g24,g16)
    c: Coincident(g25,g26)
    c: Coincident(g26,g27)
    c: Coincident(g27,g25)
    c: Coincident(g28,g29)
    c: Coincident(g29,g30)
    c: Coincident(g30,g31)
    c: Coincident(g31,g32)
    c: Coincident(g32,g33)
    c: Coincident(g33,g34)
    c: Coincident(g34,g35)
    c: Coincident(g35,g36)
    c: Coincident(g36,g37)
    c: Coincident(g37,g38)
    c: Coincident(g38,g39)
    c: Coincident(g39,g40)
    c: Coincident(g40,g41)
    c: Coincident(g41,g42)
    c: Coincident(g42,g43)
    c: Coincident(g43,g44)
    c: Coincident(g44,g45)
    c: Coincident(g45,g46)
    c: Coincident(g46,g47)
    c: Coincident(g47,g48)
    c: Coincident(g48,g49)
    c: Coincident(g49,g28)
    c: Coincident(g50,g51)
    c: Coincident(g51,g52)
    c: Coincident(g52,g53)
    c: Coincident(g53,g54)
    c: Coincident(g54,g55)
    c: Coincident(g55,g56)
    c: Coincident(g56,g57)
    c: Coincident(g57,g58)
    c: Coincident(g58,g59)
    c: Coincident(g59,g60)
    c: Coincident(g60,g61)
    c: Coincident(g61,g50)
    c: Coincident(g62,g63)
    c: Coincident(g63,g64)
    c: Coincident(g64,g65)
    c: Coincident(g65,g66)
    c: Coincident(g66,g67)
    c: Coincident(g67,g68)
    c: Coincident(g68,g69)
    c: Coincident(g69,g70)
    c: Coincident(g70,g71)
    c: Coincident(g71,g62)
FEATURE [PartDesign::Pad] Pad001  label="GratulererPad"
  BaseFeature = -> Pad
  Direction = (0,0,1)
  Length = 2
  Length2 = 10
  Profile = -> Sketch
  ReferenceAxis = -> Sketch [N_Axis]
  Type = 0
  expr: Length = Spreadsheet.dim_text_h
FEATURE [PartDesign::Pad] Pad002  label="MedPad"
  BaseFeature = -> Pad001
  Direction = (0,0,1)
  Length = 2
  Length2 = 10
  Profile = -> Sketch002
  ReferenceAxis = -> Sketch002 [N_Axis]
  Type = 0
  expr: Length = Spreadsheet.dim_text_h
FEATURE [PartDesign::Pad] Pad003  label="DagenPad"
  BaseFeature = -> Pad002
  Direction = (0,0,1)
  Length = 2
  Length2 = 10
  Profile = -> Sketch003
  ReferenceAxis = -> Sketch003 [N_Axis]
  Type = 0
  expr: Length = Spreadsheet.dim_text_h
FEATURE [PartDesign::Body] Body
  Group = -> [DatumPlane,Sketch001,Pad,Sketch,Sketch002,Sketch003,Pad001,Pad002,Pad003]
  Origin = -> Origin
  Tip = -> Pad003
FEATURE [Mesh::Feature] Mesh  label="Body (Meshed)"
